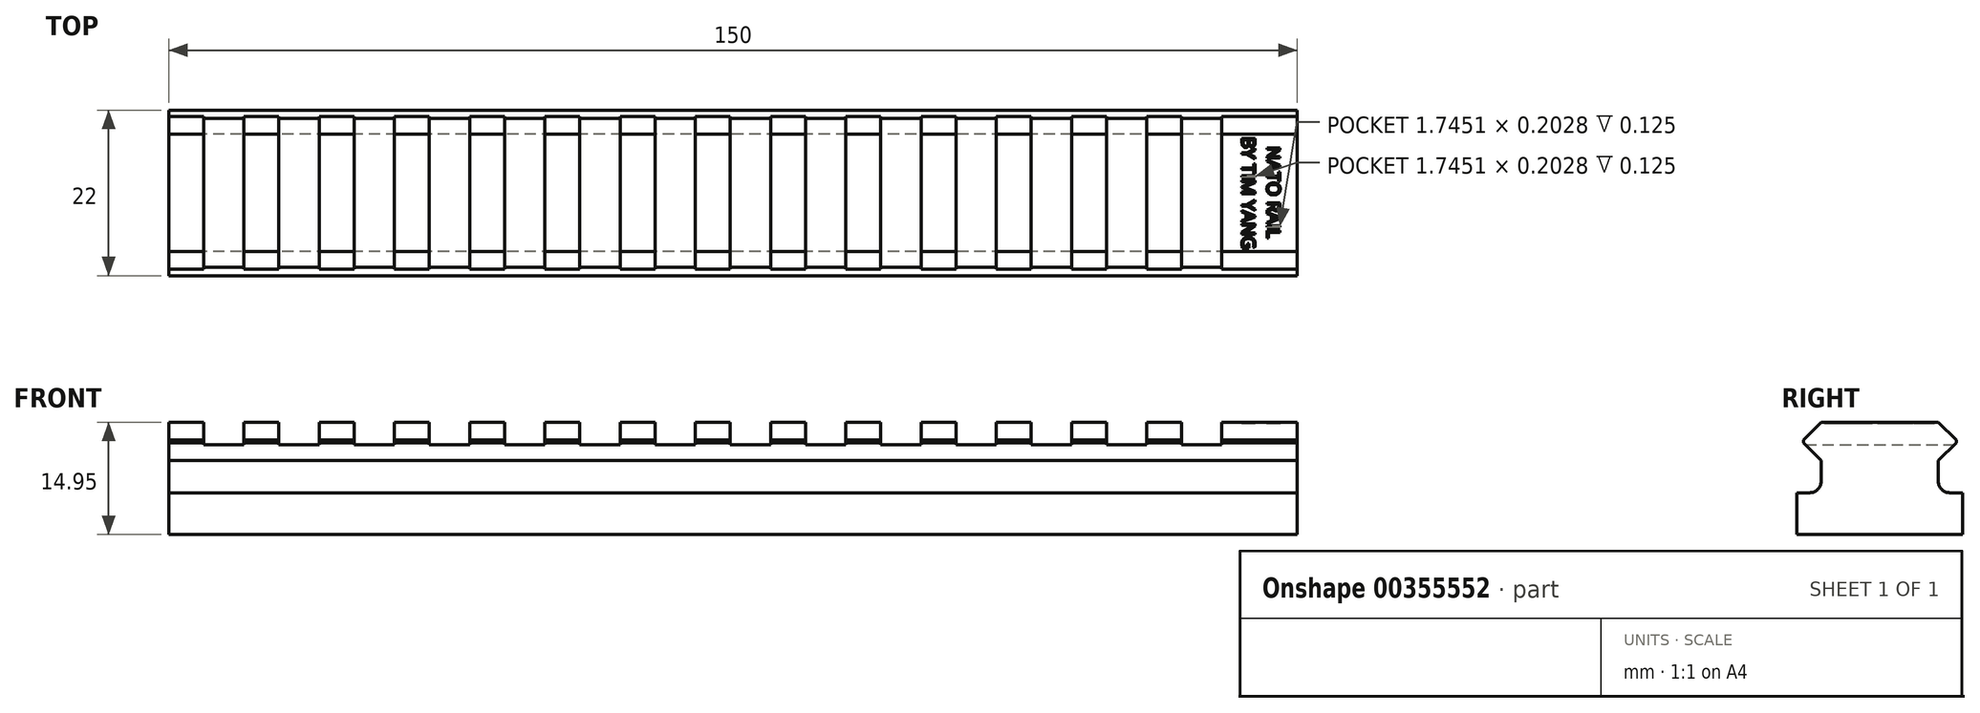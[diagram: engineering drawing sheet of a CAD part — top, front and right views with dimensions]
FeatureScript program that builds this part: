
annotation { "Feature Type Name" : "Feature", "Feature Type Description" : "" }
export const myFeature = defineFeature(function(context is Context, id is Id, definition is map)
    precondition{}
    {
        {
            var Q0;
            Q0=qCreatedBy(makeId("Right.planeOp"),FACE);
            var sketch = newSketch(context, id + "F0", { "sketchPlane" : qUnion([Q0])});
            skLineSegment(sketch, "E0.bottom", {"start": v(8.98, 1.42) * mm, "end": v(-8.98, 1.42) * mm, "construction": true});
            skLineSegment(sketch, "E0.top", {"start": v(8.98, 4.16) * mm, "end": v(-8.98, 4.16) * mm, "construction": true});
            skLineSegment(sketch, "E0.left", {"start": v(8.98, 1.42) * mm, "end": v(8.98, 4.16) * mm, "construction": true});
            skLineSegment(sketch, "E0.right", {"start": v(-8.98, 1.42) * mm, "end": v(-8.98, 4.16) * mm, "construction": true});
            skPoint(sketch, "E0.middle", {"position": v(0, 2.8) * mm});
            skLineSegment(sketch, "E1", {"start": v(-7.8, 5.34) * mm, "end": v(-10.16, 2.98) * mm});
            skPoint(sketch, "E2", {"position": v(-8.98, 4.16) * mm});
            skLineSegment(sketch, "E3", {"start": v(-10.16, 2.6) * mm, "end": v(-7.8, 0.24) * mm});
            skLineSegment(sketch, "E4", {"start": v(7.8, 5.34) * mm, "end": v(10.16, 2.98) * mm});
            skLineSegment(sketch, "E5", {"start": v(10.16, 2.6) * mm, "end": v(7.8, 0.24) * mm});
            skPoint(sketch, "E6", {"position": v(8.98, 4.16) * mm});
            skPoint(sketch, "E7", {"position": v(8.98, 1.42) * mm});
            skPoint(sketch, "E8", {"position": v(-8.98, 1.42) * mm});
            skLineSegment(sketch, "E9", {"start": v(-7.8, 5.34) * mm, "end": v(7.8, 5.34) * mm});
            skLineSegment(sketch, "E10", {"start": v(-10.16, 2.98) * mm, "end": v(-10.16, 2.6) * mm});
            skLineSegment(sketch, "E11", {"start": v(10.16, 2.98) * mm, "end": v(10.16, 2.6) * mm});
            skLineSegment(sketch, "E12", {"start": v(-7.8, 0.24) * mm, "end": v(-7.8, -2.56) * mm});
            skLineSegment(sketch, "E13", {"start": v(7.8, 0.24) * mm, "end": v(7.8, -2.56) * mm});
            skLineSegment(sketch, "E14.bottom", {"start": v(11, -4.06) * mm, "end": v(9.3, -4.06) * mm});
            skLineSegment(sketch, "E14.top", {"start": v(11, -9.61) * mm, "end": v(-11, -9.61) * mm});
            skLineSegment(sketch, "E14.left", {"start": v(11, -4.06) * mm, "end": v(11, -9.61) * mm});
            skLineSegment(sketch, "E14.right", {"start": v(-11, -4.06) * mm, "end": v(-11, -9.61) * mm});
            skPoint(sketch, "E14.middle", {"position": v(0, -6.84) * mm});
            skPoint(sketch, "E15.newPointA", {"position": v(7.8, -4.06) * mm});
            skArc(sketch, "E15.filletArc", {"start": v(7.8, -2.56) * mm, "mid": v(8.24, -3.62) * mm, "end": v(9.3, -4.06) * mm});
            skLineSegment(sketch, "E16", {"start": v(-9.3, -4.06) * mm, "end": v(-11, -4.06) * mm});
            skPoint(sketch, "E17.visualSharp", {"position": v(-7.8, -4.06) * mm});
            skArc(sketch, "E17.filletArc", {"start": v(-9.3, -4.06) * mm, "mid": v(-8.24, -3.62) * mm, "end": v(-7.8, -2.56) * mm});
            skSolve(sketch);
        }
        {
            var Q0;
            Q0 = qSketchRegion(id + "F0", true);
            extrude(context, id + "F1", {"entities" : qUnion([Q0]), "endBound" : BoundingType.SYMMETRIC, "depth" : 150 * mm});
        }
        {
            var Q0;
            Q0=makeQuery(id+"F1.opExtrude","SWEPT_FACE",FACE,{"disambiguationData":[OSD([sQuery(id+"F0.wireOp",EDGE,"E9")])]});
            var sketch = newSketch(context, id + "F2", { "sketchPlane" : qUnion([Q0])});
            skLineSegment(sketch, "E18.bottom", {"start": v(-65, -10.16) * mm, "end": v(-70.35, -10.16) * mm});
            skLineSegment(sketch, "E18.top", {"start": v(-65, 10.16) * mm, "end": v(-70.35, 10.16) * mm});
            skLineSegment(sketch, "E18.left", {"start": v(-65, -10.16) * mm, "end": v(-65, 10.16) * mm});
            skLineSegment(sketch, "E18.right", {"start": v(-70.35, -10.16) * mm, "end": v(-70.35, 10.16) * mm});
            skPoint(sketch, "E18.middle", {"position": v(-67.67, 0) * mm});
            skPoint(sketch, "E19.1.0.0", {"position": v(-57.67, 0) * mm});
            skLineSegment(sketch, "E19.1.0.1", {"start": v(-55, -10.16) * mm, "end": v(-60.35, -10.16) * mm});
            skLineSegment(sketch, "E19.1.0.2", {"start": v(-55, 10.16) * mm, "end": v(-60.35, 10.16) * mm});
            skLineSegment(sketch, "E19.1.0.3", {"start": v(-55, -10.16) * mm, "end": v(-55, 10.16) * mm});
            skLineSegment(sketch, "E19.1.0.4", {"start": v(-60.35, -10.16) * mm, "end": v(-60.35, 10.16) * mm});
            skPoint(sketch, "E19.2.0.0", {"position": v(-47.67, 0) * mm});
            skLineSegment(sketch, "E19.2.0.1", {"start": v(-45, -10.16) * mm, "end": v(-50.35, -10.16) * mm});
            skLineSegment(sketch, "E19.2.0.2", {"start": v(-45, 10.16) * mm, "end": v(-50.35, 10.16) * mm});
            skLineSegment(sketch, "E19.2.0.3", {"start": v(-45, -10.16) * mm, "end": v(-45, 10.16) * mm});
            skLineSegment(sketch, "E19.2.0.4", {"start": v(-50.35, -10.16) * mm, "end": v(-50.35, 10.16) * mm});
            skPoint(sketch, "E19.3.0.0", {"position": v(-37.67, 0) * mm});
            skLineSegment(sketch, "E19.3.0.1", {"start": v(-35, -10.16) * mm, "end": v(-40.35, -10.16) * mm});
            skLineSegment(sketch, "E19.3.0.2", {"start": v(-35, 10.16) * mm, "end": v(-40.35, 10.16) * mm});
            skLineSegment(sketch, "E19.3.0.3", {"start": v(-35, -10.16) * mm, "end": v(-35, 10.16) * mm});
            skLineSegment(sketch, "E19.3.0.4", {"start": v(-40.35, -10.16) * mm, "end": v(-40.35, 10.16) * mm});
            skPoint(sketch, "E19.4.0.0", {"position": v(-27.67, 0) * mm});
            skLineSegment(sketch, "E19.4.0.1", {"start": v(-25, -10.16) * mm, "end": v(-30.35, -10.16) * mm});
            skLineSegment(sketch, "E19.4.0.2", {"start": v(-25, 10.16) * mm, "end": v(-30.35, 10.16) * mm});
            skLineSegment(sketch, "E19.4.0.3", {"start": v(-25, -10.16) * mm, "end": v(-25, 10.16) * mm});
            skLineSegment(sketch, "E19.4.0.4", {"start": v(-30.35, -10.16) * mm, "end": v(-30.35, 10.16) * mm});
            skPoint(sketch, "E19.5.0.0", {"position": v(-17.67, 0) * mm});
            skLineSegment(sketch, "E19.5.0.1", {"start": v(-15, -10.16) * mm, "end": v(-20.35, -10.16) * mm});
            skLineSegment(sketch, "E19.5.0.2", {"start": v(-15, 10.16) * mm, "end": v(-20.35, 10.16) * mm});
            skLineSegment(sketch, "E19.5.0.3", {"start": v(-15, -10.16) * mm, "end": v(-15, 10.16) * mm});
            skLineSegment(sketch, "E19.5.0.4", {"start": v(-20.35, -10.16) * mm, "end": v(-20.35, 10.16) * mm});
            skPoint(sketch, "E19.6.0.0", {"position": v(-7.67, 0) * mm});
            skLineSegment(sketch, "E19.6.0.1", {"start": v(-5, -10.16) * mm, "end": v(-10.35, -10.16) * mm});
            skLineSegment(sketch, "E19.6.0.2", {"start": v(-5, 10.16) * mm, "end": v(-10.35, 10.16) * mm});
            skLineSegment(sketch, "E19.6.0.3", {"start": v(-5, -10.16) * mm, "end": v(-5, 10.16) * mm});
            skLineSegment(sketch, "E19.6.0.4", {"start": v(-10.35, -10.16) * mm, "end": v(-10.35, 10.16) * mm});
            skPoint(sketch, "E19.7.0.0", {"position": v(2.33, 0) * mm});
            skLineSegment(sketch, "E19.7.0.1", {"start": v(5, -10.16) * mm, "end": v(-0.35, -10.16) * mm});
            skLineSegment(sketch, "E19.7.0.2", {"start": v(5, 10.16) * mm, "end": v(-0.35, 10.16) * mm});
            skLineSegment(sketch, "E19.7.0.3", {"start": v(5, -10.16) * mm, "end": v(5, 10.16) * mm});
            skLineSegment(sketch, "E19.7.0.4", {"start": v(-0.35, -10.16) * mm, "end": v(-0.35, 10.16) * mm});
            skPoint(sketch, "E19.8.0.0", {"position": v(12.33, 0) * mm});
            skLineSegment(sketch, "E19.8.0.1", {"start": v(15, -10.16) * mm, "end": v(9.65, -10.16) * mm});
            skLineSegment(sketch, "E19.8.0.2", {"start": v(15, 10.16) * mm, "end": v(9.65, 10.16) * mm});
            skLineSegment(sketch, "E19.8.0.3", {"start": v(15, -10.16) * mm, "end": v(15, 10.16) * mm});
            skLineSegment(sketch, "E19.8.0.4", {"start": v(9.65, -10.16) * mm, "end": v(9.65, 10.16) * mm});
            skPoint(sketch, "E19.9.0.0", {"position": v(22.33, 0) * mm});
            skLineSegment(sketch, "E19.9.0.1", {"start": v(25, -10.16) * mm, "end": v(19.65, -10.16) * mm});
            skLineSegment(sketch, "E19.9.0.2", {"start": v(25, 10.16) * mm, "end": v(19.65, 10.16) * mm});
            skLineSegment(sketch, "E19.9.0.3", {"start": v(25, -10.16) * mm, "end": v(25, 10.16) * mm});
            skLineSegment(sketch, "E19.9.0.4", {"start": v(19.65, -10.16) * mm, "end": v(19.65, 10.16) * mm});
            skPoint(sketch, "E19.10.0.0", {"position": v(32.33, 0) * mm});
            skLineSegment(sketch, "E19.10.0.1", {"start": v(35, -10.16) * mm, "end": v(29.65, -10.16) * mm});
            skLineSegment(sketch, "E19.10.0.2", {"start": v(35, 10.16) * mm, "end": v(29.65, 10.16) * mm});
            skLineSegment(sketch, "E19.10.0.3", {"start": v(35, -10.16) * mm, "end": v(35, 10.16) * mm});
            skLineSegment(sketch, "E19.10.0.4", {"start": v(29.65, -10.16) * mm, "end": v(29.65, 10.16) * mm});
            skPoint(sketch, "E19.11.0.0", {"position": v(42.33, 0) * mm});
            skLineSegment(sketch, "E19.11.0.1", {"start": v(45, -10.16) * mm, "end": v(39.65, -10.16) * mm});
            skLineSegment(sketch, "E19.11.0.2", {"start": v(45, 10.16) * mm, "end": v(39.65, 10.16) * mm});
            skLineSegment(sketch, "E19.11.0.3", {"start": v(45, -10.16) * mm, "end": v(45, 10.16) * mm});
            skLineSegment(sketch, "E19.11.0.4", {"start": v(39.65, -10.16) * mm, "end": v(39.65, 10.16) * mm});
            skPoint(sketch, "E19.12.0.0", {"position": v(52.33, 0) * mm});
            skLineSegment(sketch, "E19.12.0.1", {"start": v(55, -10.16) * mm, "end": v(49.65, -10.16) * mm});
            skLineSegment(sketch, "E19.12.0.2", {"start": v(55, 10.16) * mm, "end": v(49.65, 10.16) * mm});
            skLineSegment(sketch, "E19.12.0.3", {"start": v(55, -10.16) * mm, "end": v(55, 10.16) * mm});
            skLineSegment(sketch, "E19.12.0.4", {"start": v(49.65, -10.16) * mm, "end": v(49.65, 10.16) * mm});
            skPoint(sketch, "E19.13.0.0", {"position": v(62.33, 0) * mm});
            skLineSegment(sketch, "E19.13.0.1", {"start": v(65, -10.16) * mm, "end": v(59.65, -10.16) * mm});
            skLineSegment(sketch, "E19.13.0.2", {"start": v(65, 10.16) * mm, "end": v(59.65, 10.16) * mm});
            skLineSegment(sketch, "E19.13.0.3", {"start": v(65, -10.16) * mm, "end": v(65, 10.16) * mm});
            skLineSegment(sketch, "E19.13.0.4", {"start": v(59.65, -10.16) * mm, "end": v(59.65, 10.16) * mm});
            skLineSegment(sketch, "E19.direction1", {"start": v(-70.35, -10.16) * mm, "end": v(-60.35, -10.16) * mm, "construction": true});
            skSolve(sketch);
        }
        {
            var Q0;
            Q0 = qSketchRegion(id + "F2", true);
            extrude(context, id + "F3", {"entities" : qUnion([Q0]), "operationType" : NewBodyOperationType.REMOVE, "oppositeDirection" : true, "depth" : 3 * mm});
        }
        {
            var Q0;
            {var subQ1=sQuery(id+"F0.wireOp",EDGE,"E9");Q0=makeQuery(id+"F3.boolean.opBoolean","SPLIT",FACE,{"disambiguationData":[TD([makeQuery(id+"F3.opExtrude","SWEPT_FACE",FACE,{"disambiguationData":[OSD([sQuery(id+"F2.wireOp",EDGE,"E19.13.0.3")])]})])],"derivedFrom":makeQuery(id+"F1.opExtrude","SWEPT_FACE",FACE,{"disambiguationData":[OSD([subQ1])]})});}
            var sketch = newSketch(context, id + "F4", { "sketchPlane" : qUnion([Q0])});
            skText(sketch, "E20", { "text": "  NATO RAIL\nBY TIM YANG", "fontName": "OpenSans-Regular.ttf"});
            const initialGuessF4  = {"E20": [0.07099, 0.0075, 0, -1, 0.00176]};
            skSetInitialGuess(sketch, initialGuessF4);
            skSolve(sketch);
        }
        {
            var Q0;
            Q0 = qSketchRegion(id + "F4", true);
            extrude(context, id + "F5", {"entities" : qUnion([Q0]), "operationType" : NewBodyOperationType.REMOVE, "oppositeDirection" : true, "depth" : .125 * mm});
        }
    });
